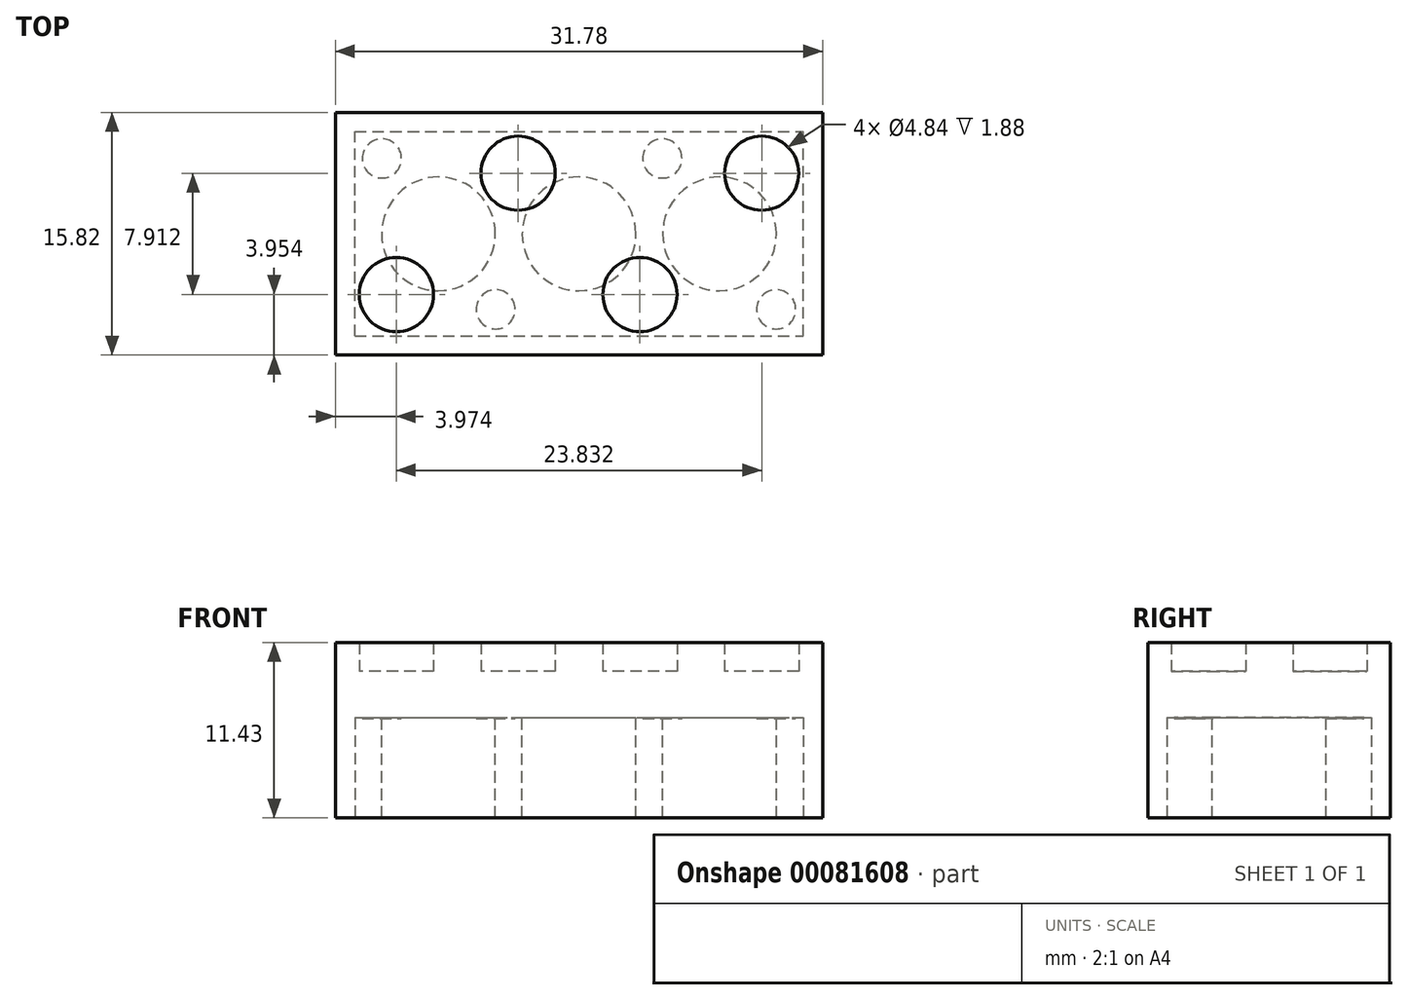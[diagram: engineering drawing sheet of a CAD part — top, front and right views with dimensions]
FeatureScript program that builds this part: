
annotation { "Feature Type Name" : "Feature", "Feature Type Description" : "" }
export const myFeature = defineFeature(function(context is Context, id is Id, definition is map)
    precondition{}
    {
        {
            var Q0;
            Q0=qCreatedBy(makeId("Top.planeOp"),FACE);
            var sketch = newSketch(context, id + "F0", { "sketchPlane" : qUnion([Q0])});
            skLineSegment(sketch, "E0.bottom", {"start": v(-15.89, 7.91) * mm, "end": v(15.89, 7.91) * mm});
            skLineSegment(sketch, "E0.top", {"start": v(-15.89, -7.91) * mm, "end": v(15.89, -7.91) * mm});
            skLineSegment(sketch, "E0.left", {"start": v(-15.89, 7.91) * mm, "end": v(-15.89, -7.91) * mm});
            skLineSegment(sketch, "E0.right", {"start": v(15.89, 7.91) * mm, "end": v(15.89, -7.91) * mm});
            skPoint(sketch, "E0.middle", {"position": v(0, 0) * mm});
            skSolve(sketch);
        }
        {
            var Q0;
            Q0=makeQuery(id+"F0.imprint","IMPRINT",FACE,{"disambiguationData":[TD([[makeQuery(id+"F0.imprint","IMPRINT",EDGE,{"derivedFrom":sQuery(id+"F0.wireOp",EDGE,"E0.bottom")}),-1.0]])]});
            extrude(context, id + "F1", {"entities" : qUnion([Q0]), "depth" : 9.55 * mm});
        }
        {
            var Q0;
            Q0=makeQuery(id+"F1.opExtrude","CAP_FACE",FACE,{"disambiguationData":[OSD([sQuery(id+"F0.wireOp",EDGE,"E0.bottom"),sQuery(id+"F0.wireOp",EDGE,"E0.top"),sQuery(id+"F0.wireOp",EDGE,"E0.left"),sQuery(id+"F0.wireOp",EDGE,"E0.right")])],"isStart":false});
            var sketch = newSketch(context, id + "F2", { "sketchPlane" : qUnion([Q0])});
            skCircle(sketch, "E1", {"center": v(-11.92, 3.96) * mm, "radius": 2.42 * mm});
            skCircle(sketch, "E2.MirrorC", {"center": v(-3.97, 3.96) * mm, "radius": 2.42 * mm});
            skCircle(sketch, "E3.MirrorC", {"center": v(-11.92, -3.96) * mm, "radius": 2.42 * mm});
            skCircle(sketch, "E4.MirrorC", {"center": v(-3.97, -3.96) * mm, "radius": 2.42 * mm});
            skCircle(sketch, "E5.MirrorC", {"center": v(3.97, 3.96) * mm, "radius": 2.42 * mm});
            skCircle(sketch, "E6.MirrorC", {"center": v(11.92, 3.96) * mm, "radius": 2.42 * mm});
            skCircle(sketch, "E7.MirrorC", {"center": v(11.92, -3.96) * mm, "radius": 2.42 * mm});
            skCircle(sketch, "E8.MirrorC", {"center": v(3.97, -3.96) * mm, "radius": 2.42 * mm});
            skSolve(sketch);
        }
        {
            var Q0;
            Q0=makeQuery(id+"F2.imprint","IMPRINT",FACE,{"disambiguationData":[TD([[makeQuery(id+"F2.imprint","IMPRINT",EDGE,{"derivedFrom":sQuery(id+"F2.wireOp",EDGE,"E1")}),1.0]])]});
            var Q1;
            Q1=makeQuery(id+"F2.imprint","IMPRINT",FACE,{"disambiguationData":[TD([[makeQuery(id+"F2.imprint","IMPRINT",EDGE,{"derivedFrom":sQuery(id+"F2.wireOp",EDGE,"E2.MirrorC")}),-1.0]])]});
            var Q2;
            Q2=makeQuery(id+"F2.imprint","IMPRINT",FACE,{"disambiguationData":[TD([[makeQuery(id+"F2.imprint","IMPRINT",EDGE,{"derivedFrom":sQuery(id+"F2.wireOp",EDGE,"E5.MirrorC")}),1.0]])]});
            var Q3;
            Q3=makeQuery(id+"F2.imprint","IMPRINT",FACE,{"disambiguationData":[TD([[makeQuery(id+"F2.imprint","IMPRINT",EDGE,{"derivedFrom":sQuery(id+"F2.wireOp",EDGE,"E6.MirrorC")}),-1.0]])]});
            var Q4;
            Q4=makeQuery(id+"F2.imprint","IMPRINT",FACE,{"disambiguationData":[TD([[makeQuery(id+"F2.imprint","IMPRINT",EDGE,{"derivedFrom":sQuery(id+"F2.wireOp",EDGE,"E7.MirrorC")}),1.0]])]});
            var Q5;
            Q5=makeQuery(id+"F2.imprint","IMPRINT",FACE,{"disambiguationData":[TD([[makeQuery(id+"F2.imprint","IMPRINT",EDGE,{"derivedFrom":sQuery(id+"F2.wireOp",EDGE,"E8.MirrorC")}),-1.0]])]});
            var Q6;
            Q6=makeQuery(id+"F2.imprint","IMPRINT",FACE,{"disambiguationData":[TD([[makeQuery(id+"F2.imprint","IMPRINT",EDGE,{"derivedFrom":sQuery(id+"F2.wireOp",EDGE,"E4.MirrorC")}),1.0]])]});
            var Q7;
            Q7=makeQuery(id+"F2.imprint","IMPRINT",FACE,{"disambiguationData":[TD([[makeQuery(id+"F2.imprint","IMPRINT",EDGE,{"derivedFrom":sQuery(id+"F2.wireOp",EDGE,"E3.MirrorC")}),-1.0]])]});
            extrude(context, id + "F3", {"entities" : qUnion([Q0, Q1, Q2, Q3, Q4, Q5, Q6, Q7]), "operationType" : NewBodyOperationType.ADD, "depth" : 1.88 * mm});
        }
        {
            var Q0;
            Q0=makeQuery(id+"F1.opExtrude","CAP_FACE",FACE,{"disambiguationData":[OSD([sQuery(id+"F0.wireOp",EDGE,"E0.bottom"),sQuery(id+"F0.wireOp",EDGE,"E0.top"),sQuery(id+"F0.wireOp",EDGE,"E0.left"),sQuery(id+"F0.wireOp",EDGE,"E0.right")])],"isStart":true});
            var sketch = newSketch(context, id + "F4", { "sketchPlane" : qUnion([Q0])});
            skLineSegment(sketch, "E9", {"start": v(-15.89, 2.31) * mm, "end": v(-14.64, 2.31) * mm});
            skLineSegment(sketch, "E10", {"start": v(-12.3, 7.91) * mm, "end": v(-12.3, 6.67) * mm});
            skLineSegment(sketch, "E11.bottom", {"start": v(-14.63, 6.68) * mm, "end": v(14.63, 6.68) * mm});
            skLineSegment(sketch, "E11.top", {"start": v(-14.63, -6.68) * mm, "end": v(14.63, -6.68) * mm});
            skLineSegment(sketch, "E11.left", {"start": v(-14.63, 6.68) * mm, "end": v(-14.63, -6.68) * mm});
            skLineSegment(sketch, "E11.right", {"start": v(14.63, 6.68) * mm, "end": v(14.63, -6.68) * mm});
            skPoint(sketch, "E11.middle", {"position": v(0, 0) * mm});
            skSolve(sketch);
        }
        {
            var Q0;
            Q0=makeQuery(id+"F4.imprint","IMPRINT",FACE,{"disambiguationData":[TD([[makeQuery(id+"F4.imprint","IMPRINT",EDGE,{"derivedFrom":sQuery(id+"F4.wireOp",EDGE,"E11.top")}),1.0]])]});
            extrude(context, id + "F5", {"entities" : qUnion([Q0]), "operationType" : NewBodyOperationType.REMOVE, "oppositeDirection" : true, "depth" : 6.48 * mm});
        }
        {
            var Q0;
            Q0=makeQuery(id+"F5.boolean.opBoolean","COPY",FACE,{"derivedFrom":makeQuery(id+"F5.opExtrude","CAP_FACE",FACE,{"disambiguationData":[OSD([sQuery(id+"F4.wireOp",EDGE,"E11.bottom"),sQuery(id+"F4.wireOp",EDGE,"E11.top"),sQuery(id+"F4.wireOp",EDGE,"E11.left"),sQuery(id+"F4.wireOp",EDGE,"E11.right")])],"isStart":false})});
            var sketch = newSketch(context, id + "F6", { "sketchPlane" : qUnion([Q0])});
            skCircle(sketch, "E12", {"center": v(0, 0) * mm, "radius": 3.7 * mm});
            skCircle(sketch, "E13", {"center": v(9.17, 0) * mm, "radius": 3.7 * mm});
            skCircle(sketch, "E14", {"center": v(-9.17, 0) * mm, "radius": 3.7 * mm});
            skLineSegment(sketch, "E15", {"start": v(0, 6.68) * mm, "end": v(0, 3.7) * mm});
            skLineSegment(sketch, "E16", {"start": v(0, -3.7) * mm, "end": v(0, -6.68) * mm});
            skSolve(sketch);
        }
        {
            var Q0;
            Q0=makeQuery(id+"F6.imprint","IMPRINT",FACE,{"disambiguationData":[TD([[makeQuery(id+"F6.imprint","IMPRINT",EDGE,{"derivedFrom":sQuery(id+"F6.wireOp",EDGE,"E14")}),1.0]])]});
            var Q1;
            {var subQ0=sQuery(id+"F6.wireOp",EDGE,"E12");var subQ1=makeQuery(id+"F6.imprint","INTERSECT",VERTEX,{"derivedFrom":[subQ0,sQuery(id+"F6.wireOp",EDGE,"E15")]});Q1=makeQuery(id+"F6.imprint","IMPRINT",FACE,{"disambiguationData":[TD([[makeQuery(id+"F6.imprint","IMPRINT",EDGE,{"disambiguationData":[TD([[subQ1,-1.0]])],"derivedFrom":subQ0}),1.0]])]});}
            var Q2;
            Q2=makeQuery(id+"F6.imprint","IMPRINT",FACE,{"disambiguationData":[TD([[makeQuery(id+"F6.imprint","IMPRINT",EDGE,{"derivedFrom":sQuery(id+"F6.wireOp",EDGE,"E13")}),1.0]])]});
            extrude(context, id + "F7", {"entities" : qUnion([Q0, Q1, Q2]), "operationType" : NewBodyOperationType.ADD, "depth" : 6.48 * mm});
        }
        {
            var Q0;
            Q0=makeQuery(id+"F5.boolean.opBoolean","COPY",FACE,{"derivedFrom":makeQuery(id+"F5.opExtrude","CAP_FACE",FACE,{"disambiguationData":[OSD([sQuery(id+"F4.wireOp",EDGE,"E11.bottom"),sQuery(id+"F4.wireOp",EDGE,"E11.top"),sQuery(id+"F4.wireOp",EDGE,"E11.left"),sQuery(id+"F4.wireOp",EDGE,"E11.right")])],"isStart":false})});
            var sketch = newSketch(context, id + "F8", { "sketchPlane" : qUnion([Q0])});
            skCircle(sketch, "E17", {"center": v(-12.86, 4.92) * mm, "radius": 1.28 * mm});
            skCircle(sketch, "E18.MirrorC", {"center": v(-5.44, 4.92) * mm, "radius": 1.28 * mm});
            skCircle(sketch, "E19.MirrorC", {"center": v(-5.44, -4.92) * mm, "radius": 1.28 * mm});
            skCircle(sketch, "E20.MirrorC", {"center": v(-12.86, -4.92) * mm, "radius": 1.28 * mm});
            skCircle(sketch, "E21.MirrorC", {"center": v(5.44, 4.92) * mm, "radius": 1.28 * mm});
            skCircle(sketch, "E22.MirrorC", {"center": v(12.86, 4.92) * mm, "radius": 1.28 * mm});
            skCircle(sketch, "E23.MirrorC", {"center": v(5.44, -4.92) * mm, "radius": 1.28 * mm});
            skCircle(sketch, "E24.MirrorC", {"center": v(12.86, -4.92) * mm, "radius": 1.28 * mm});
            skLineSegment(sketch, "E25", {"start": v(0, 6.68) * mm, "end": v(0, 3.7) * mm});
            skLineSegment(sketch, "E26", {"start": v(0, -3.7) * mm, "end": v(0, -6.68) * mm});
            skSolve(sketch);
        }
        {
            var Q0;
            Q0=makeQuery(id+"F8.imprint","IMPRINT",FACE,{"disambiguationData":[TD([[makeQuery(id+"F8.imprint","IMPRINT",EDGE,{"derivedFrom":sQuery(id+"F8.wireOp",EDGE,"E17")}),1.0]])]});
            var Q1;
            Q1=makeQuery(id+"F8.imprint","IMPRINT",FACE,{"disambiguationData":[TD([[makeQuery(id+"F8.imprint","IMPRINT",EDGE,{"derivedFrom":sQuery(id+"F8.wireOp",EDGE,"E18.MirrorC")}),-1.0]])]});
            var Q2;
            Q2=makeQuery(id+"F8.imprint","IMPRINT",FACE,{"disambiguationData":[TD([[makeQuery(id+"F8.imprint","IMPRINT",EDGE,{"derivedFrom":sQuery(id+"F8.wireOp",EDGE,"E21.MirrorC")}),1.0]])]});
            var Q3;
            Q3=makeQuery(id+"F8.imprint","IMPRINT",FACE,{"disambiguationData":[TD([[makeQuery(id+"F8.imprint","IMPRINT",EDGE,{"derivedFrom":sQuery(id+"F8.wireOp",EDGE,"E22.MirrorC")}),-1.0]])]});
            var Q4;
            Q4=makeQuery(id+"F8.imprint","IMPRINT",FACE,{"disambiguationData":[TD([[makeQuery(id+"F8.imprint","IMPRINT",EDGE,{"derivedFrom":sQuery(id+"F8.wireOp",EDGE,"E24.MirrorC")}),1.0]])]});
            var Q5;
            Q5=makeQuery(id+"F8.imprint","IMPRINT",FACE,{"disambiguationData":[TD([[makeQuery(id+"F8.imprint","IMPRINT",EDGE,{"derivedFrom":sQuery(id+"F8.wireOp",EDGE,"E23.MirrorC")}),-1.0]])]});
            var Q6;
            Q6=makeQuery(id+"F8.imprint","IMPRINT",FACE,{"disambiguationData":[TD([[makeQuery(id+"F8.imprint","IMPRINT",EDGE,{"derivedFrom":sQuery(id+"F8.wireOp",EDGE,"E19.MirrorC")}),1.0]])]});
            var Q7;
            Q7=makeQuery(id+"F8.imprint","IMPRINT",FACE,{"disambiguationData":[TD([[makeQuery(id+"F8.imprint","IMPRINT",EDGE,{"derivedFrom":sQuery(id+"F8.wireOp",EDGE,"E20.MirrorC")}),-1.0]])]});
            extrude(context, id + "F9", {"entities" : qUnion([Q0, Q1, Q2, Q3, Q4, Q5, Q6, Q7]), "operationType" : NewBodyOperationType.REMOVE, "oppositeDirection" : true, "depth" : 0.05 * mm});
        }
    });
